# Revit family: RN 57026 Optifitt-Press-Schiebemuffe
name_source: partatom
category: Rohrformteile
units: mm (PartAtom-declared; Revit-internal decimal feet)

## family parameters
Arbeitsebenenbasiert = Nein
Beim Laden mit Abzugskörper schneiden = Nein
Bemaßung runder Anschluss = Durchmesser verwenden
Gemeinsam genutzt = Nein
Immer vertikal = Ja
Teiletyp = Verbindung

## types (4) — shared parameters
1.010.00.2 Blattnummer der Richtlinie = 29
1.010.00.3 Ausgabedatum (Monat) der Richtlinie = 201308
1.010.00.4 Herstellername = R. Nussbaum AG
1.010.00.5 Revisionsdatum der Datei = 20190521
1.010.00.6 Webadresse des Herstellers = http://www.nussbaum.ch
1.100.00.4 Produktbezeichnung = Versorgung
1.110.00.2 Index = 2
1.110.00.4 Produktbezeichnung = Optifitt-Press
1.960/3L.00.8 Link (URL) = https://www.nussbaum.ch
29.700.00.4 Produktname = Optifitt-Press-Schiebemuffe, mit Einsteckende
29.700.00.5 Produktkennung = 2
29.700.00.6 Querschnittsform = 1
29.700.00.7 Nennweitensystem = DN
29.700.00.8 Nenndrucksystem = PN
29.710.02.4 Nenndruck = 16
29.710.02.5 max. zul. Überdruck [hPa] = 1600
29.710.02.7 max. zul. Dauer-Betriebsdruck [hPa] = 1600
29.710.02.9 max. zul. Dauer-Betriebstemperatur [°C] = 95
Beschreibung = Optifitt-Press-Schiebemuffe
CONNECTOR0_dX_00 = 86 mm  [stored 0.282152 ft]
Connector Visibility = Nein
EnclosingSpace Visibility = Nein
Hersteller = R. Nussbaum AG
URL = https://www.nussbaum.ch

## per-type parameters (varying)
| type | 1.800.00.3 TGA-Nummer | 1.800.00.4 Kommentarfeld | 1.810.00.3 Hersteller-Bestellnummer | 1.810.00.4 DATANORM-Nummer | 1.810.00.6 GTIN-Nummer | 29.710.02.10 Formstück-Gewicht [kg] | 29.710.02.3 Benennung | CONNECTOR0_DIAMETER_dX_0r | CONNECTOR0_dX_01 | CONNECTOR0_ref_dX | CONNECTOR1_DIAMETER_dX_0r | CONNECTOR1_dX_00 | CONNECTOR1_dX_01 | CONNECTOR1_ref_dX | Modell | R. Nussbaum AG 57026.22 de Visibility | R. Nussbaum AG 57026.23 de Visibility | R. Nussbaum AG 57026.24 de Visibility | R. Nussbaum AG 57026.25 de Visibility | Typenkommentare |
| DN=25 | 01900200000000000000000000000000000000000000000025000000000000000004 | 57026.25, Optifitt-Press-Schiebemuffe, mit Einsteckende, DN=25, L=173 | 57026.25 | 57026.25 | 7612945816603 | 0.451 | Optifitt-Press-Schiebemuffe, mit Einsteckende, DN=25, L=173 | 25 mm  [stored 0.082021 ft] | 34 mm | 34 mm | 25 mm  [stored 0.082021 ft] | 139 mm | 173 mm | 139 mm | 57026.25 | Nein | Nein | Nein | Ja | Optifitt-Press-Schiebemuffe  DN=25 |
| DN=20 | 01900200000000000000000000000000000000000000000025000000000000000003 | 57026.24, Optifitt-Press-Schiebemuffe, mit Einsteckende, DN=20, L=152 | 57026.24 | 57026.24 | 7612945816597 | 0.3 | Optifitt-Press-Schiebemuffe, mit Einsteckende, DN=20, L=152 | 20 mm | 29 mm | 29 mm | 20 mm | 123 mm | 152 mm | 123 mm | 57026.24 | Nein | Nein | Ja | Nein | Optifitt-Press-Schiebemuffe  DN=20 |
| DN=15 | 01900200000000000000000000000000000000000000000025000000000000000002 | 57026.23, Optifitt-Press-Schiebemuffe, mit Einsteckende, DN=15, L=123 | 57026.23 | 57026.23 | 7612945816580 | 0.198 | Optifitt-Press-Schiebemuffe, mit Einsteckende, DN=15, L=123 | 15 mm | 27 mm | 27 mm | 15 mm | 96 mm | 123 mm | 96 mm | 57026.23 | Nein | Ja | Nein | Nein | Optifitt-Press-Schiebemuffe  DN=15 |
| DN=10 | 01900200000000000000000000000000000000000000000025000000000000000001 | 57026.22, Optifitt-Press-Schiebemuffe, mit Einsteckende, DN=10, L=110 | 57026.22 | 57026.22 | 7612945816573 | 0.12 | Optifitt-Press-Schiebemuffe, mit Einsteckende, DN=10, L=110 | 12 mm  [stored 0.0393701 ft] | 110 mm | 86 mm  [stored 0.282152 ft] | 12 mm  [stored 0.0393701 ft] | 86 mm  [stored 0.282152 ft] | 110 mm | 86 mm  [stored 0.282152 ft] | 57026.22 | Ja | Nein | Nein | Nein | Optifitt-Press-Schiebemuffe  DN=10 |

note: [stored X ft] marks values corroborated as IEEE doubles in the binary element streams (Revit-internal decimal feet)

## geometry (parser evidence)
native form markers: Sweep x2
no freeform markers — native parametric forms only
